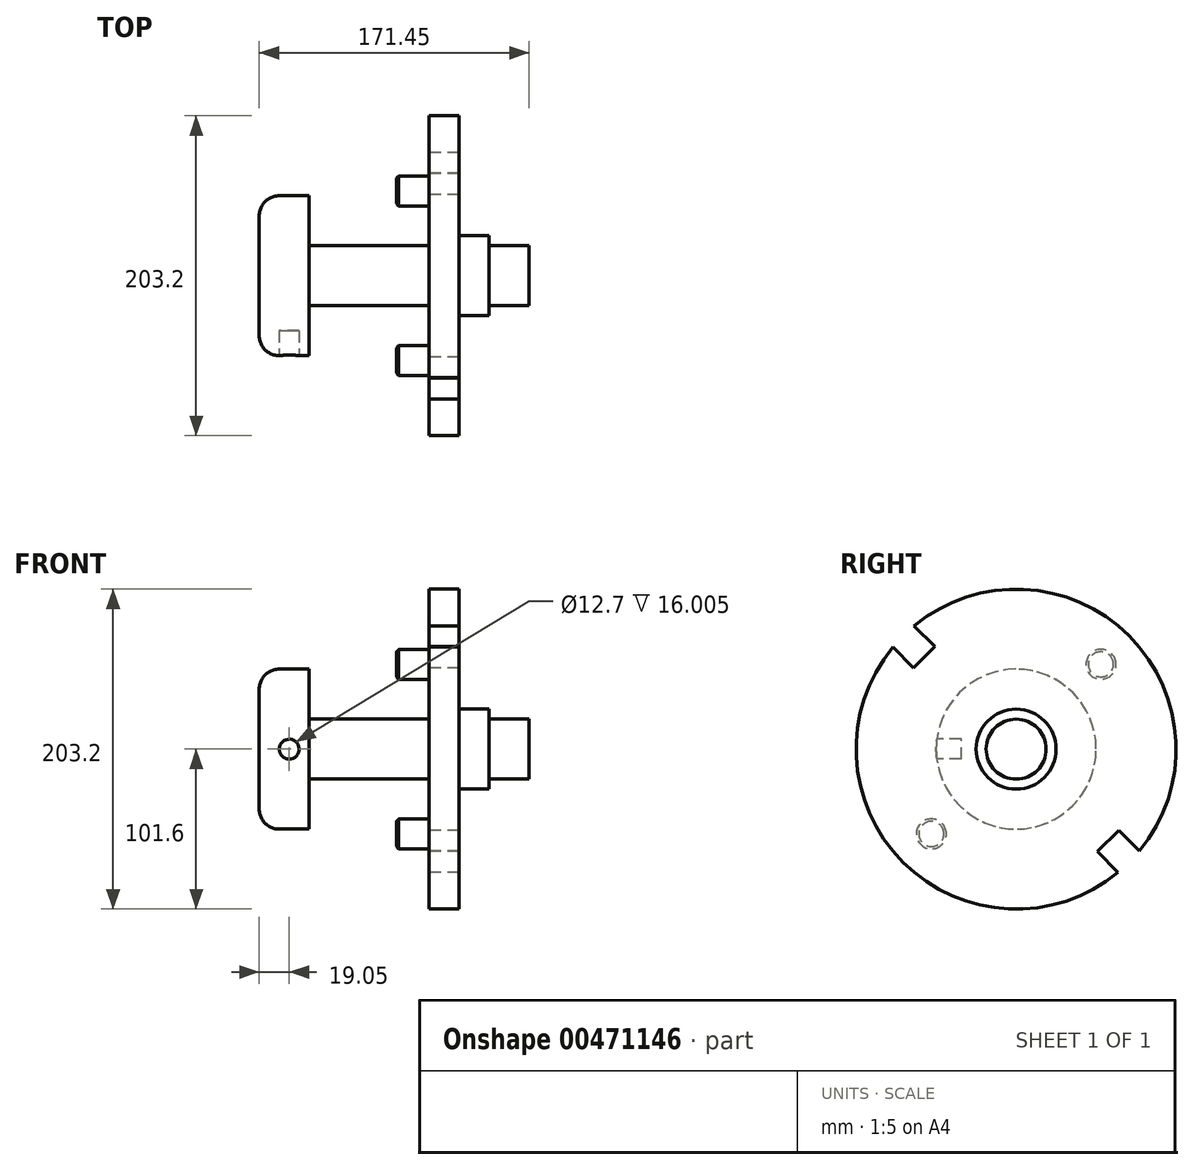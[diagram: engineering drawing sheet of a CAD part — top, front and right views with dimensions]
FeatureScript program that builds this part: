
annotation { "Feature Type Name" : "Feature", "Feature Type Description" : "" }
export const myFeature = defineFeature(function(context is Context, id is Id, definition is map)
    precondition{}
    {
        {
            var Q0;
            Q0=qCreatedBy(makeId("Front.planeOp"),FACE);
            var sketch = newSketch(context, id + "F0", { "sketchPlane" : qUnion([Q0])});
            skLineSegment(sketch, "E0", {"start": v(0, 0) * mm, "end": v(0, 38.1) * mm});
            skLineSegment(sketch, "E1", {"start": v(12.7, 50.8) * mm, "end": v(31.75, 50.8) * mm});
            skPoint(sketch, "E2.visualSharp", {"position": v(0, 50.8) * mm});
            skArc(sketch, "E2.filletArc", {"start": v(12.7, 50.8) * mm, "mid": v(3.72, 47.08) * mm, "end": v(0, 38.1) * mm});
            skLineSegment(sketch, "E3", {"start": v(107.95, 19.05) * mm, "end": v(31.75, 19.05) * mm});
            skLineSegment(sketch, "E4", {"start": v(107.95, 19.05) * mm, "end": v(107.95, 101.6) * mm});
            skPoint(sketch, "E4.endSnap0", {"position": v(107.95, 0) * mm});
            skLineSegment(sketch, "E5", {"start": v(127, 101.6) * mm, "end": v(107.95, 101.6) * mm});
            skLineSegment(sketch, "E6", {"start": v(127, 25.4) * mm, "end": v(146.05, 25.4) * mm});
            skLineSegment(sketch, "E7", {"start": v(146.05, 19.05) * mm, "end": v(171.45, 19.05) * mm});
            skLineSegment(sketch, "E8", {"start": v(0, 0) * mm, "end": v(171.45, 0) * mm});
            skPoint(sketch, "E9.start.orphan", {"position": v(31.75, 0) * mm});
            skLineSegment(sketch, "E10.trimOffspring", {"start": v(31.75, 19.05) * mm, "end": v(31.75, 50.8) * mm});
            skPoint(sketch, "E11.start.orphan", {"position": v(127, 0) * mm});
            skLineSegment(sketch, "E12.trimOffspring", {"start": v(127, 25.4) * mm, "end": v(127, 101.6) * mm});
            skLineSegment(sketch, "E13.trimOffspring", {"start": v(146.05, 19.05) * mm, "end": v(146.05, 25.4) * mm});
            skLineSegment(sketch, "E14", {"start": v(171.45, 19.05) * mm, "end": v(171.45, 0) * mm});
            skSolve(sketch);
        }
        {
            var Q0;
            Q0=makeQuery(id+"F0.imprint","IMPRINT",FACE,{"disambiguationData":[TD([[makeQuery(id+"F0.imprint","IMPRINT",EDGE,{"derivedFrom":sQuery(id+"F0.wireOp",EDGE,"E0")}),-1.0]])]});
            var Q1;
            Q1=sQuery(id+"F0.wireOp",EDGE,"E8");
            revolve(context, id + "F1", {"entities" : qUnion([Q0]), "axis" : qUnion([Q1]), "revolveType" : RevolveType.FULL});
        }
        {
            var Q0;
            Q0=qCreatedBy(makeId("Front.planeOp"),FACE);
            cPlane(context, id + "F2", {"entities" : qUnion([Q0]), "cplaneType" : CPlaneType.OFFSET, "offset" : 50.8 * mm, "width" : 152.4 * mm, "height" : 152.4 * mm});
        }
        {
            var Q0;
            Q0=qCreatedBy(id+"F2.planeOp",FACE);
            var sketch = newSketch(context, id + "F3", { "sketchPlane" : qUnion([Q0])});
            skLineSegment(sketch, "E15", {"start": v(12.7, 50.8) * mm, "end": v(31.75, 50.8) * mm});
            skLineSegment(sketch, "E16", {"start": v(31.75, -50.8) * mm, "end": v(12.7, -50.8) * mm});
            skCircle(sketch, "E17", {"center": v(19.05, 0) * mm, "radius": 6.35 * mm});
            skSolve(sketch);
        }
        {
            var Q0;
            Q0=makeQuery(id+"F3.imprint","IMPRINT",FACE,{"disambiguationData":[TD([[makeQuery(id+"F3.imprint","IMPRINT",EDGE,{"derivedFrom":sQuery(id+"F3.wireOp",EDGE,"E17")}),1.0]])]});
            extrude(context, id + "F4", {"entities" : qUnion([Q0]), "operationType" : NewBodyOperationType.REMOVE, "oppositeDirection" : true, "depth" : 16 * mm});
        }
        {
            var Q0;
            Q0=makeQuery(id+"F1.opRevolve","SWEPT_FACE",FACE,{"disambiguationData":[OSD([sQuery(id+"F0.wireOp",EDGE,"E4")])]});
            var sketch = newSketch(context, id + "F5", { "sketchPlane" : qUnion([Q0])});
            skLineSegment(sketch, "E18", {"start": v(0, 0) * mm, "end": v(119.18, 0) * mm, "construction": true});
            skLineSegment(sketch, "E19", {"start": v(0, 0) * mm, "end": v(97.27, 97.27) * mm, "construction": true});
            skLineSegment(sketch, "E20.bottom", {"start": v(78.58, 92.05) * mm, "end": v(51.64, 65.1) * mm});
            skLineSegment(sketch, "E20.top", {"start": v(92.05, 78.58) * mm, "end": v(65.1, 51.64) * mm});
            skLineSegment(sketch, "E20.left", {"start": v(78.58, 92.05) * mm, "end": v(92.05, 78.58) * mm});
            skLineSegment(sketch, "E20.right", {"start": v(51.64, 65.1) * mm, "end": v(65.1, 51.64) * mm});
            skPoint(sketch, "E20.middle", {"position": v(71.84, 71.84) * mm});
            skLineSegment(sketch, "E21.1.0", {"start": v(-92.05, -78.58) * mm, "end": v(-65.1, -51.64) * mm});
            skLineSegment(sketch, "E21.1.1", {"start": v(-51.64, -65.1) * mm, "end": v(-65.1, -51.64) * mm});
            skLineSegment(sketch, "E21.1.2", {"start": v(-78.58, -92.05) * mm, "end": v(-51.64, -65.1) * mm});
            skLineSegment(sketch, "E21.1.3", {"start": v(-78.58, -92.05) * mm, "end": v(-92.05, -78.58) * mm});
            skPoint(sketch, "E21.center", {"position": v(0, 0) * mm});
            skSolve(sketch);
        }
        {
            var Q0;
            {var subQ0=sQuery(id+"F5.wireOp",EDGE,"E21.1.3");Q0=makeQuery(id+"F5.imprint","IMPRINT",FACE,{"disambiguationData":[TD([[makeQuery(id+"F5.imprint","IMPRINT",EDGE,{"derivedFrom":subQ0}),-1.0]])]});}
            var Q1;
            {var subQ0=sQuery(id+"F5.wireOp",EDGE,"E21.1.1");Q1=makeQuery(id+"F5.imprint","IMPRINT",FACE,{"disambiguationData":[TD([[makeQuery(id+"F5.imprint","IMPRINT",EDGE,{"derivedFrom":subQ0}),1.0]])]});}
            var Q2;
            {var subQ0=sQuery(id+"F5.wireOp",EDGE,"E20.right");Q2=makeQuery(id+"F5.imprint","IMPRINT",FACE,{"disambiguationData":[TD([[makeQuery(id+"F5.imprint","IMPRINT",EDGE,{"derivedFrom":subQ0}),1.0]])]});}
            var Q3;
            {var subQ0=sQuery(id+"F5.wireOp",EDGE,"E20.left");Q3=makeQuery(id+"F5.imprint","IMPRINT",FACE,{"disambiguationData":[TD([[makeQuery(id+"F5.imprint","IMPRINT",EDGE,{"derivedFrom":subQ0}),-1.0]])]});}
            extrude(context, id + "F6", {"entities" : qUnion([Q0, Q1, Q2, Q3]), "operationType" : NewBodyOperationType.REMOVE, "oppositeDirection" : true, "depth" : 25.4 * mm});
        }
        {
            var Q0;
            Q0=makeQuery(id+"F1.opRevolve","SWEPT_FACE",FACE,{"disambiguationData":[OSD([sQuery(id+"F0.wireOp",EDGE,"E4")])]});
            var sketch = newSketch(context, id + "F7", { "sketchPlane" : qUnion([Q0])});
            skLineSegment(sketch, "E22", {"start": v(0, 0) * mm, "end": v(70.6, -70.6) * mm, "construction": true});
            skLineSegment(sketch, "E23", {"start": v(0, 0) * mm, "end": v(0, -69.94) * mm, "construction": true});
            skCircle(sketch, "E24", {"center": v(53.88, -53.88) * mm, "radius": 9.53 * mm});
            skCircle(sketch, "E25.1.0", {"center": v(-53.88, 53.88) * mm, "radius": 9.53 * mm});
            skPoint(sketch, "E25.center", {"position": v(0, 0) * mm});
            skSolve(sketch);
        }
        {
            var Q0;
            Q0=makeQuery(id+"F7.imprint","IMPRINT",FACE,{"disambiguationData":[TD([[makeQuery(id+"F7.imprint","IMPRINT",EDGE,{"derivedFrom":sQuery(id+"F7.wireOp",EDGE,"E24")}),1.0]])]});
            var Q1;
            Q1=makeQuery(id+"F7.imprint","IMPRINT",FACE,{"disambiguationData":[TD([[makeQuery(id+"F7.imprint","IMPRINT",EDGE,{"derivedFrom":sQuery(id+"F7.wireOp",EDGE,"E25.1.0")}),1.0]])]});
            extrude(context, id + "F8", {"entities" : qUnion([Q0, Q1]), "operationType" : NewBodyOperationType.ADD, "depth" : 20.83 * mm});
        }
        {
            var Q0;
            Q0=makeQuery(id+"F8.opExtrude","CAP_FACE",FACE,{"disambiguationData":[OSD([sQuery(id+"F7.wireOp",EDGE,"E25.1.0")])],"isStart":false});
            var Q1;
            Q1=makeQuery(id+"F8.opExtrude","CAP_FACE",FACE,{"disambiguationData":[OSD([sQuery(id+"F7.wireOp",EDGE,"E24")])],"isStart":false});
            chamfer(context, id + "F9", {"entities" : qUnion([Q0, Q1]), "width" : 1.52 * mm, "tangentPropagation" : true});
        }
    });
